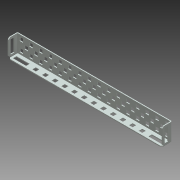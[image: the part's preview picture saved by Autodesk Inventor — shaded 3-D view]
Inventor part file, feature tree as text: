
AUTODESK INVENTOR PART (.ipt)
format: ipt  version: 2013 (Build 170138000, 138)  size: 709,120 bytes
history: native  units: mm (DEFAULTED — no unit token found)
features: other x75, extrude x67, sketch x12, sheet_metal_op x7, pattern_linear x3
ambient origin geometry x8: Origin, YZ Plane, XZ Plane, XY Plane, X Axis, Y Axis, Z Axis, Center Point
bodies: Solid1 (feature_tree)
feature tree (164):
  sheet_metal_op  "Face1"
  sheet_metal_op  "Flange5"
  sheet_metal_op  "Flange6"
  other  "Corner Chamfer2"
  sheet_metal_op  "Flange7"
  other  "Corner Chamfer3"
  pattern_linear  "Rectangular Pattern1"  Count1=15 Spacing1=12.7mm
  pattern_linear  "Rectangular Pattern2"  Spacing1=11.5316mm  [1 undecoded]
  pattern_linear  "Rectangular Pattern3"  Spacing1=1.1684mm  [1 undecoded]
  sketch  "Sketch17"  dims[d65=0.5842mm]
  sketch  "Sketch18"  dims[d66=2.3368mm]
  sketch  "Sketch19"  dims[d67=0.381mm d68=11.5316mm d69=90.0deg d70=0.381mm d71=1.1684mm d72=0.5842mm d73=2.3368mm d74=0.381mm d75=11.5316mm d76=90.0deg d77=0.381mm d84=1.905mm d85=6.35mm d86=45.0deg d88=17.272mm d89=2.794mm d90=2.794mm d91=4.572mm d92=4.572mm d93=8.128mm d94=120.0mm d96=12.7mm d97=10.0mm d99=25.4mm d102=8.128mm d103=2.794mm d104=1.1684mm d105=0.5842mm d106=2.3368mm d107=0.381mm d108=11.5316mm d109=90.0deg d110=0.381mm d111=4.572mm d112=2.794mm d113=1.1684mm d114=0.0mm d115=1.905mm d116=6.35mm d117=45.0deg d118=2.794mm d119=2.794mm d121=17.272mm d122=4.572mm d123=1.1684mm d124=0.0mm d125=25.4mm d126=0.0mm d127=160.0mm d129=12.7mm d130=20.0mm d132=12.7mm d133=25.4mm d134=0.0mm d135=150.0mm d137=12.7mm d138=25.4mm d139=0.0mm d140=120.0mm d142=12.7mm d143=0.0mm d144=0.0mm d145=0.0mm d146=0.0mm d147=0.0mm d148=0.0mm d149=0.0mm d150=0.0mm d151=0.0mm d152=0.0mm d153=0.0mm d154=0.0mm d155=0.0mm d156=0.0mm d157=0.0mm d158=0.0mm d159=0.0mm d160=0.0mm d161=0.0mm d162=0.0mm d163=0.0mm d164=0.0mm d165=0.0mm d166=0.0mm d167=0.0mm d168=0.0mm d169=0.0mm d170=0.0mm d171=0.0mm d172=0.0mm d173=0.0mm d174=0.0mm d175=0.0mm d176=0.0mm d177=0.0mm d178=0.0mm d179=0.0mm d180=0.0mm d181=0.0mm d182=0.0mm d183=0.0mm d184=0.0mm d185=0.0mm d186=0.0mm d187=0.0mm d188=0.0mm d189=0.0mm d190=6.35mm d191=9.144mm d192=0.0mm d193=0.0mm d194=0.0mm d195=0.0mm d196=0.0mm d197=0.0mm d198=0.0mm d199=0.0mm d200=0.0mm d201=0.0mm d202=0.0mm d203=0.0mm d204=0.0mm d205=0.0mm d206=0.0mm d207=0.0mm d208=0.0mm d209=0.0mm d210=0.0mm d211=0.0mm d212=0.0mm d213=0.0mm d214=0.0mm d215=0.0mm d216=0.0mm d217=0.0mm d218=0.0mm d219=0.0mm d220=0.0mm d221=0.0mm d222=0.0mm d223=0.0mm d224=0.0mm d225=0.0mm d226=0.0mm d227=0.0mm d228=0.0mm d229=0.0mm d230=0.0mm d231=0.0mm d232=0.0mm d233=0.0mm d234=0.0mm d235=0.0mm d236=0.0mm d237=0.0mm d238=0.0mm d239=0.0mm d240=0.0mm d241=0.0mm d242=0.0mm d243=0.0mm d244=0.0mm d245=0.0mm d246=0.0mm d247=0.0mm d248=0.0mm d249=0.0mm d250=0.0mm d251=0.0mm d252=0.0mm d253=0.0mm d254=0.0mm d255=0.0mm d256=0.0mm d257=0.0mm d258=0.0mm d259=0.0mm d260=0.0mm d261=0.0mm d262=0.0mm d263=25.4mm d264=0.0mm d265=25.4mm d266=0.0mm d267=25.4mm d268=0.0mm d269=25.4mm d270=0.0mm d271=0.0mm d272=0.0mm d273=0.0mm d274=0.0mm d275=0.0mm d276=0.0mm d277=0.0mm d278=0.0mm d279=25.4mm d280=0.0mm d281=25.4mm d282=0.0mm d283=25.4mm d284=0.0mm d285=25.4mm d286=0.0mm d287=0.0mm d288=0.0mm d289=0.0mm d290=0.0mm d291=0.0mm d292=0.0mm d293=0.0mm d294=0.0mm]
  sketch  "Sketch1"  dims[d20=2.794mm]
  other  "Plate1"
  sketch  "Sketch7"  dims[d21=2.794mm]
  other  "Plate6"
  sheet_metal_op  "Bend5"
  sketch  "Sketch8"  dims[d22=2.921mm]
  other  "Plate7"
  sheet_metal_op  "Bend6"
  sketch  "Sketch11"  dims[d23=22.86mm]
  sketch  "Sketch12"  dims[d24=4.6228mm]
  other  "Plate8"
  sheet_metal_op  "Bend7"
  sketch  "Sketch13"  dims[d25=8.128mm]
  sketch  "Sketch14"  dims[d26=4.6228mm]
  other  "Srf1"
  other  "Srf2"
  other  "Srf3"
  other  "Srf4"
  other  "Srf5"
  other  "Srf6"
  other  "Srf7"
  other  "Srf8"
  other  "Srf9"
  other  "Srf10"
  other  "Srf11"
  other  "Srf12"
  other  "Srf13"
  other  "Srf14"
  other  "Srf15"
  other  "Srf16"
  other  "Srf17"
  other  "Srf18"
  other  "Srf19"
  other  "Srf20"
  other  "Srf21"
  other  "Srf22"
  other  "Srf23"
  other  "Srf24"
  other  "Srf25"
  other  "Srf26"
  other  "Srf27"
  other  "Srf28"
  other  "Srf29"
  other  "Srf30"
  other  "Srf31"
  other  "Srf32"
  sketch  "Sketch15"  dims[d27=0.381mm]
  other  "Srf33"
  other  "Srf34"
  other  "Srf35"
  other  "Srf36"
  other  "Srf37"
  other  "Srf38"
  other  "Srf39"
  other  "Srf40"
  other  "Srf41"
  other  "Srf42"
  other  "Srf43"
  other  "Srf44"
  other  "Srf45"
  other  "Srf46"
  other  "Srf47"
  sketch  "Sketch16"  dims[d64=1.1684mm]
  other  "Srf48"
  other  "Srf49"
  other  "Srf50"
  other  "Srf51"
  other  "Srf52"
  other  "Srf53"
  other  "Srf54"
  other  "Srf55"
  other  "Srf56"
  other  "Srf57"
  other  "Srf58"
  other  "Srf59"
  other  "Srf60"
  other  "Srf61"
  other  "Srf62"
  other  "Srf63"
  other  "Srf64"
  other  "Srf65"
  other  "Srf66"
  other  "Srf67"
  other  "Cut2"
  other  "Cut3"
  extrude  "ExtrusionSrf1"  Depth=0.5842mm
  extrude  "ExtrusionSrf33"  Depth=2.3368mm
  extrude  "ExtrusionSrf48"  Depth=0.381mm
  extrude  "ExtrusionSrf60"  Depth=11.5316mm TaperAngle=90.0deg
  extrude  "ExtrusionSrf61"  Depth=1.905mm TaperAngle=45.0deg
  extrude  "ExtrusionSrf62"  Depth=17.272mm
  extrude  "ExtrusionSrf63"  Depth=2.794mm
  extrude  "ExtrusionSrf64"  Depth=2.794mm
  extrude  "ExtrusionSrf65"  Depth=4.572mm
  extrude  "ExtrusionSrf66"  Depth=4.572mm
  extrude  "ExtrusionSrf67"  Depth=8.128mm
  extrude  "ExtrusionSrf2"  Depth=120.0mm
  extrude  "ExtrusionSrf3"  Depth=8.128mm
  extrude  "ExtrusionSrf4"  Depth=2.794mm
  extrude  "ExtrusionSrf5"  Depth=1.1684mm
  extrude  "ExtrusionSrf6"  Depth=0.5842mm
  extrude  "ExtrusionSrf7"  Depth=2.3368mm
  extrude  "ExtrusionSrf8"  Depth=0.381mm
  extrude  "ExtrusionSrf9"  Depth=11.5316mm TaperAngle=90.0deg
  extrude  "ExtrusionSrf10"  Depth=4.572mm
  extrude  "ExtrusionSrf11"  Depth=2.794mm
  extrude  "ExtrusionSrf12"  Depth=1.1684mm
  extrude  "ExtrusionSrf13"  TaperAngle=0.0deg  [1 undecoded]
  extrude  "ExtrusionSrf14"  Depth=1.905mm TaperAngle=45.0deg
  extrude  "ExtrusionSrf15"  Depth=2.794mm
  extrude  "ExtrusionSrf16"  Depth=2.794mm
  extrude  "ExtrusionSrf17"  Depth=17.272mm
  extrude  "ExtrusionSrf18"  Depth=4.572mm
  extrude  "ExtrusionSrf19"  Depth=1.1684mm
  extrude  "ExtrusionSrf20"  TaperAngle=0.0deg  [1 undecoded]
  extrude  "ExtrusionSrf21"  Depth=25.4mm TaperAngle=0.0deg
  extrude  "ExtrusionSrf22"  Depth=160.0mm
  extrude  "ExtrusionSrf23"  Depth=20.0mm
  extrude  "ExtrusionSrf24"  Depth=25.4mm TaperAngle=0.0deg
  extrude  "ExtrusionSrf25"  Depth=150.0mm
  extrude  "ExtrusionSrf26"  Depth=25.4mm TaperAngle=0.0deg
  extrude  "ExtrusionSrf27"  Depth=120.0mm
  extrude  "ExtrusionSrf28"  TaperAngle=0.0deg  [1 undecoded]
  extrude  "ExtrusionSrf29"  TaperAngle=0.0deg  [1 undecoded]
  extrude  "ExtrusionSrf30"  TaperAngle=0.0deg  [1 undecoded]
  extrude  "ExtrusionSrf31"  TaperAngle=0.0deg  [1 undecoded]
  extrude  "ExtrusionSrf32"  TaperAngle=0.0deg  [1 undecoded]
  extrude  "ExtrusionSrf34"  TaperAngle=0.0deg  [1 undecoded]
  extrude  "ExtrusionSrf35"  TaperAngle=0.0deg  [1 undecoded]
  extrude  "ExtrusionSrf36"  TaperAngle=0.0deg  [1 undecoded]
  extrude  "ExtrusionSrf37"  TaperAngle=0.0deg  [1 undecoded]
  extrude  "ExtrusionSrf38"  TaperAngle=0.0deg  [1 undecoded]
  extrude  "ExtrusionSrf39"  TaperAngle=0.0deg  [1 undecoded]
  extrude  "ExtrusionSrf40"  TaperAngle=0.0deg  [1 undecoded]
  extrude  "ExtrusionSrf41"  TaperAngle=0.0deg  [1 undecoded]
  extrude  "ExtrusionSrf42"  TaperAngle=0.0deg  [1 undecoded]
  extrude  "ExtrusionSrf43"  TaperAngle=0.0deg  [1 undecoded]
  extrude  "ExtrusionSrf44"  TaperAngle=0.0deg  [1 undecoded]
  extrude  "ExtrusionSrf45"  TaperAngle=0.0deg  [1 undecoded]
  extrude  "ExtrusionSrf46"  TaperAngle=0.0deg  [1 undecoded]
  extrude  "ExtrusionSrf47"  TaperAngle=0.0deg  [1 undecoded]
  extrude  "ExtrusionSrf49"  TaperAngle=0.0deg  [1 undecoded]
  extrude  "ExtrusionSrf50"  TaperAngle=0.0deg  [1 undecoded]
  extrude  "ExtrusionSrf51"  TaperAngle=0.0deg  [1 undecoded]
  extrude  "ExtrusionSrf52"  TaperAngle=0.0deg  [1 undecoded]
  extrude  "ExtrusionSrf53"  TaperAngle=0.0deg  [1 undecoded]
  extrude  "ExtrusionSrf54"  TaperAngle=0.0deg  [1 undecoded]
  extrude  "ExtrusionSrf55"  TaperAngle=0.0deg  [1 undecoded]
  extrude  "ExtrusionSrf56"  TaperAngle=0.0deg  [1 undecoded]
  extrude  "ExtrusionSrf57"  TaperAngle=0.0deg  [1 undecoded]
  extrude  "ExtrusionSrf58"  TaperAngle=0.0deg  [1 undecoded]
  extrude  "ExtrusionSrf59"  TaperAngle=0.0deg  [1 undecoded]
note: 34 required parameter values undecoded (feature->parameter linkage not recoverable at this tier; creation-order binding heuristic only, values carry confidence <= 0.55)
